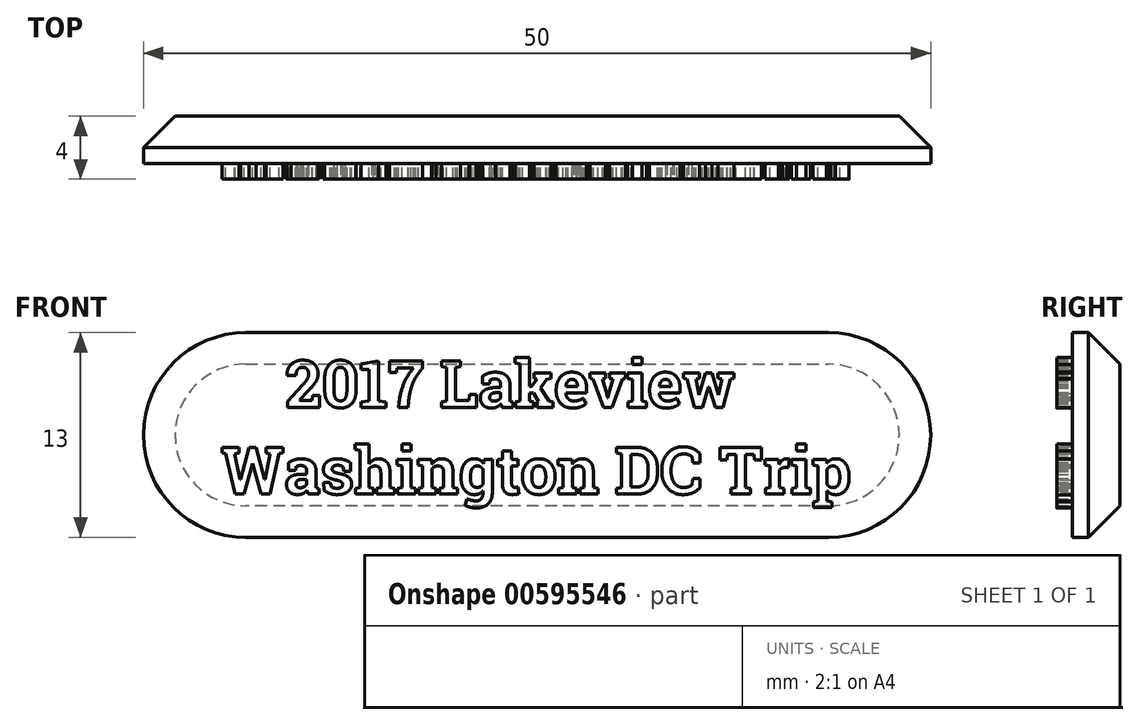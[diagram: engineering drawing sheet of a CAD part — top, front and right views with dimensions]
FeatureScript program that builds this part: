
annotation { "Feature Type Name" : "Feature", "Feature Type Description" : "" }
export const myFeature = defineFeature(function(context is Context, id is Id, definition is map)
    precondition{}
    {
        {
            var Q0;
            Q0=qCreatedBy(makeId("Front.planeOp"),FACE);
            var sketch = newSketch(context, id + "F0", { "sketchPlane" : qUnion([Q0])});
            skLineSegment(sketch, "E0.bottom", {"start": v(25, -6.5) * mm, "end": v(-25, -6.5) * mm});
            skLineSegment(sketch, "E0.top", {"start": v(25, 6.5) * mm, "end": v(-25, 6.5) * mm});
            skLineSegment(sketch, "E0.left", {"start": v(25, -6.5) * mm, "end": v(25, 6.5) * mm});
            skLineSegment(sketch, "E0.right", {"start": v(-25, -6.5) * mm, "end": v(-25, 6.5) * mm});
            skPoint(sketch, "E0.middle", {"position": v(0, 0) * mm});
            skLineSegment(sketch, "E1", {"start": v(-25, -6.5) * mm, "end": v(-12, -6.5) * mm});
            skArc(sketch, "E2", {"start": v(-25, 0) * mm, "mid": v(-23.1, -4.6) * mm, "end": v(-18.5, -6.5) * mm});
            skLineSegment(sketch, "E3", {"start": v(-25, 0) * mm, "end": v(-23, 0) * mm});
            skArc(sketch, "E4.MirrorCS", {"start": v(-25, 0) * mm, "mid": v(-23.1, 4.6) * mm, "end": v(-18.5, 6.5) * mm});
            skLineSegment(sketch, "E5.MirrorCS", {"start": v(-25, 6.5) * mm, "end": v(-12, 6.5) * mm});
            skLineSegment(sketch, "E6", {"start": v(0, 0) * mm, "end": v(0, 6.5) * mm});
            skArc(sketch, "E7.MirrorCS", {"start": v(25, 0) * mm, "mid": v(23.1, 4.6) * mm, "end": v(18.5, 6.5) * mm});
            skArc(sketch, "E8.MirrorCS", {"start": v(25, 0) * mm, "mid": v(23.1, -4.6) * mm, "end": v(18.5, -6.5) * mm});
            skLineSegment(sketch, "E9.MirrorCS", {"start": v(25, -6.5) * mm, "end": v(12, -6.5) * mm});
            skLineSegment(sketch, "E10.MirrorCS", {"start": v(25, 6.5) * mm, "end": v(12, 6.5) * mm});
            skSolve(sketch);
        }
        {
            var Q0;
            {var subQ1=sQuery(id+"F0.wireOp",EDGE,"E0.bottom");Q0=makeQuery(id+"F0.imprint","IMPRINT",FACE,{"disambiguationData":[TD([[makeQuery(id+"F0.imprint","IMPRINT",EDGE,{"derivedFrom":subQ1}),-1.0]])]});}
            extrude(context, id + "F1", {"entities" : qUnion([Q0]), "depth" : 3 * mm, "offsetDistance" : 25.4 * mm});
        }
        {
            var Q0;
            Q0=makeQuery(id+"F1.opExtrude","CAP_FACE",FACE,{"disambiguationData":[OSD([sQuery(id+"F0.wireOp",EDGE,"E0.bottom"),sQuery(id+"F0.wireOp",EDGE,"E0.top"),sQuery(id+"F0.wireOp",EDGE,"E1"),sQuery(id+"F0.wireOp",EDGE,"E2"),sQuery(id+"F0.wireOp",EDGE,"E4.MirrorCS"),sQuery(id+"F0.wireOp",EDGE,"E5.MirrorCS"),sQuery(id+"F0.wireOp",EDGE,"E7.MirrorCS"),sQuery(id+"F0.wireOp",EDGE,"E8.MirrorCS"),sQuery(id+"F0.wireOp",EDGE,"E9.MirrorCS"),sQuery(id+"F0.wireOp",EDGE,"E10.MirrorCS")])],"isStart":false});
            var sketch = newSketch(context, id + "F2", { "sketchPlane" : qUnion([Q0])});
            skText(sketch, "E11", { "text": "    2017 Lakeview\nWashington DC Trip", "fontName": "RobotoSlab-Bold.ttf"});
            skLineSegment(sketch, "E12", {"start": v(0, 4.75) * mm, "end": v(0, 6.5) * mm});
            skLineSegment(sketch, "E13", {"start": v(0, 1.75) * mm, "end": v(0, -6.5) * mm});
            skLineSegment(sketch, "E14", {"start": v(0, 0) * mm, "end": v(0, 1.75) * mm});
            const initialGuessF2  = {"E11": [-0.02008, 0.00175, 1, 0, 0.003]};
            skSetInitialGuess(sketch, initialGuessF2);
            skSolve(sketch);
        }
        {
            var Q0;
            Q0 = qSketchRegion(id + "F2", true);
            extrude(context, id + "F3", {"entities" : qUnion([Q0]), "operationType" : NewBodyOperationType.ADD, "depth" : 1 * mm, "offsetDistance" : 25 * mm});
        }
        {
            var Q0;
            Q0=makeQuery(id+"F1.opExtrude","CAP_FACE",FACE,{"disambiguationData":[OSD([sQuery(id+"F0.wireOp",EDGE,"E0.bottom"),sQuery(id+"F0.wireOp",EDGE,"E0.top"),sQuery(id+"F0.wireOp",EDGE,"E1"),sQuery(id+"F0.wireOp",EDGE,"E2"),sQuery(id+"F0.wireOp",EDGE,"E4.MirrorCS"),sQuery(id+"F0.wireOp",EDGE,"E5.MirrorCS"),sQuery(id+"F0.wireOp",EDGE,"E7.MirrorCS"),sQuery(id+"F0.wireOp",EDGE,"E8.MirrorCS"),sQuery(id+"F0.wireOp",EDGE,"E9.MirrorCS"),sQuery(id+"F0.wireOp",EDGE,"E10.MirrorCS")])],"isStart":true});
            chamfer(context, id + "F4", {"entities" : qUnion([Q0]), "width" : 2 * mm, "tangentPropagation" : true});
        }
    });
